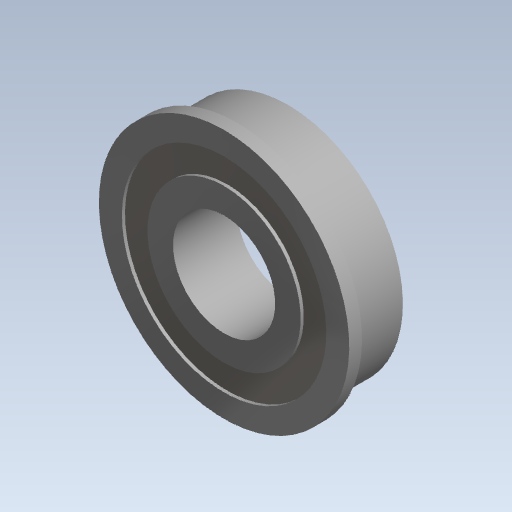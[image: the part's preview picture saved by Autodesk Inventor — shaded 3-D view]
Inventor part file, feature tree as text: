
AUTODESK INVENTOR PART (.ipt)
format: ipt  version: 2020 (Build 240168000, 168)  size: 115,712 bytes
history: native  units: mm (DEFAULTED — no unit token found)
features: revolve x1
ambient origin geometry x8: Origin, YZ Plane, XZ Plane, XY Plane, X Axis, Y Axis, Z Axis, Center Point
bodies: Solid1 (feature_tree)
feature tree (1):
  revolve  "Revolve1"  [1 undecoded]
note: 1 required parameter value undecoded (feature->parameter linkage not recoverable at this tier; creation-order binding heuristic only, values carry confidence <= 0.55)
